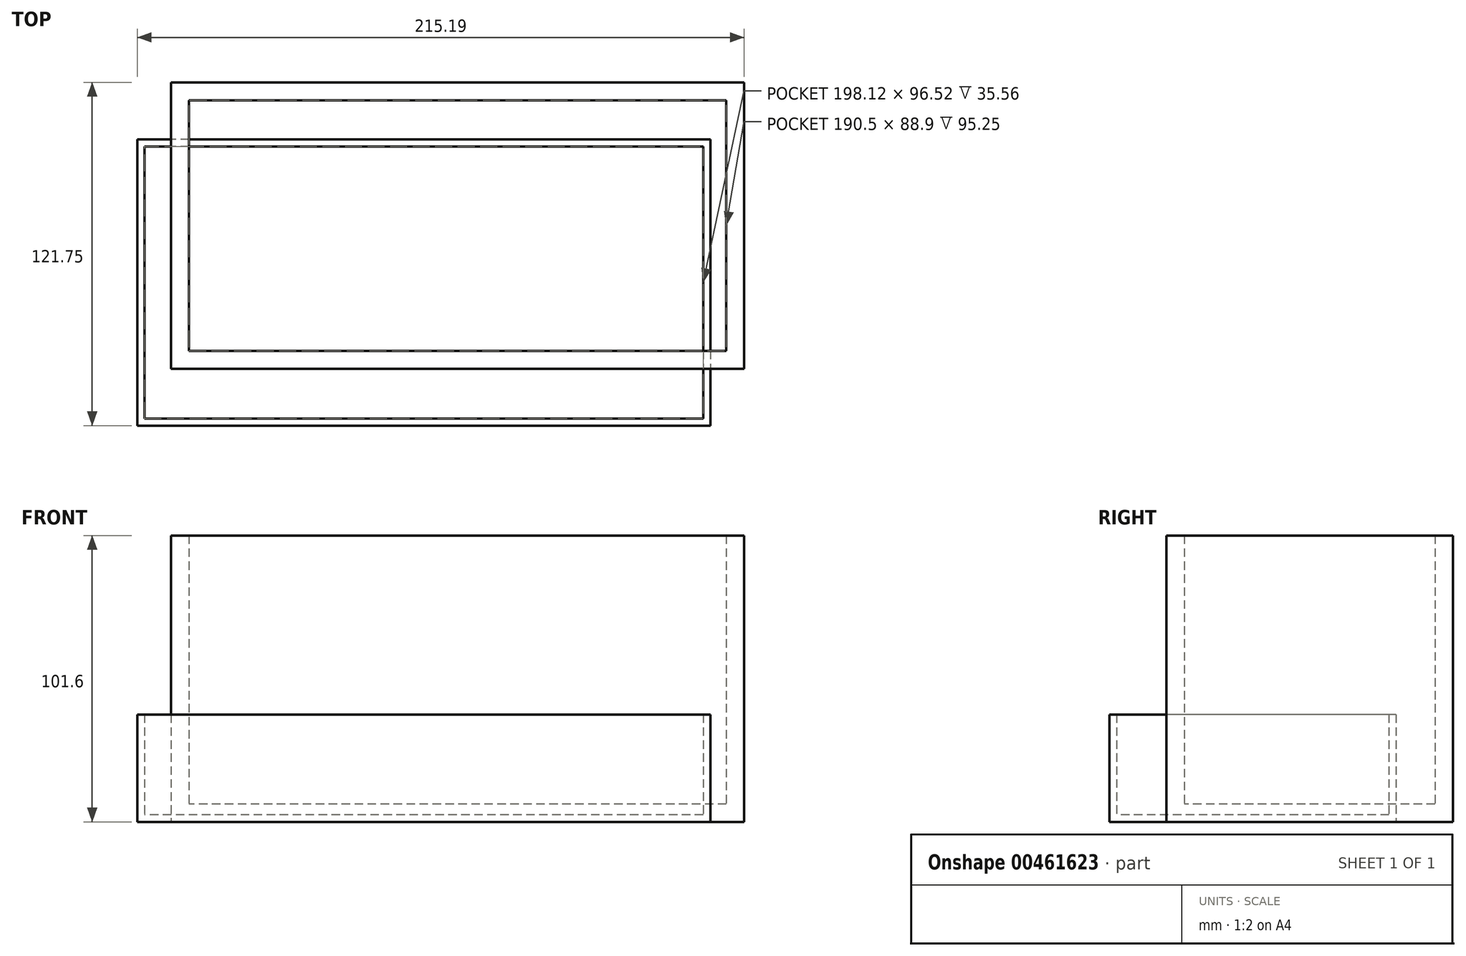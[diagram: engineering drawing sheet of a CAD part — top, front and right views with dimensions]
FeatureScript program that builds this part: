
annotation { "Feature Type Name" : "Feature", "Feature Type Description" : "" }
export const myFeature = defineFeature(function(context is Context, id is Id, definition is map)
    precondition{}
    {
        {
            var Q0;
            Q0=qCreatedBy(makeId("Top.planeOp"),FACE);
            var sketch = newSketch(context, id + "F0", { "sketchPlane" : qUnion([Q0])});
            skLineSegment(sketch, "E0.bottom", {"start": v(113.6, 70.95) * mm, "end": v(-89.6, 70.95) * mm});
            skLineSegment(sketch, "E0.top", {"start": v(113.6, -30.65) * mm, "end": v(-89.6, -30.65) * mm});
            skLineSegment(sketch, "E0.left", {"start": v(113.6, 70.95) * mm, "end": v(113.6, -30.65) * mm});
            skLineSegment(sketch, "E0.right", {"start": v(-89.6, 70.95) * mm, "end": v(-89.6, -30.65) * mm});
            skPoint(sketch, "E0.middle", {"position": v(12, 20.15) * mm});
            skSolve(sketch);
        }
        {
            var Q0;
            Q0 = qSketchRegion(id + "F0", true);
            extrude(context, id + "F1", {"entities" : qUnion([Q0]), "depth" : 101.6 * mm});
        }
        {
            var Q0;
            Q0=makeQuery(id+"F1.opExtrude","CAP_FACE",FACE,{"disambiguationData":[OSD([sQuery(id+"F0.wireOp",EDGE,"E0.bottom"),sQuery(id+"F0.wireOp",EDGE,"E0.top"),sQuery(id+"F0.wireOp",EDGE,"E0.left"),sQuery(id+"F0.wireOp",EDGE,"E0.right")])],"isStart":false});
            shell(context, id + "F2", {"entities" : qUnion([Q0]), "thickness" : 6.35 * mm});
        }
        {
            var Q0;
            Q0=qCreatedBy(makeId("Top.planeOp"),FACE);
            var sketch = newSketch(context, id + "F3", { "sketchPlane" : qUnion([Q0])});
            skLineSegment(sketch, "E1.bottom", {"start": v(101.6, 50.8) * mm, "end": v(-101.6, 50.8) * mm});
            skLineSegment(sketch, "E1.top", {"start": v(101.6, -50.8) * mm, "end": v(-101.6, -50.8) * mm});
            skLineSegment(sketch, "E1.left", {"start": v(101.6, 50.8) * mm, "end": v(101.6, -50.8) * mm});
            skLineSegment(sketch, "E1.right", {"start": v(-101.6, 50.8) * mm, "end": v(-101.6, -50.8) * mm});
            skPoint(sketch, "E1.middle", {"position": v(0, 0) * mm});
            skSolve(sketch);
        }
        {
            var Q0;
            Q0 = qSketchRegion(id + "F3", true);
            extrude(context, id + "F4", {"entities" : qUnion([Q0]), "depth" : 38.1 * mm});
        }
        {
            var Q0;
            Q0=makeQuery(id+"F4.opExtrude","CAP_FACE",FACE,{"disambiguationData":[OSD([sQuery(id+"F3.wireOp",EDGE,"E1.bottom"),sQuery(id+"F3.wireOp",EDGE,"E1.top"),sQuery(id+"F3.wireOp",EDGE,"E1.left"),sQuery(id+"F3.wireOp",EDGE,"E1.right")])],"isStart":false});
            shell(context, id + "F5", {"entities" : qUnion([Q0]), "thickness" : 2.54 * mm});
        }
    });
